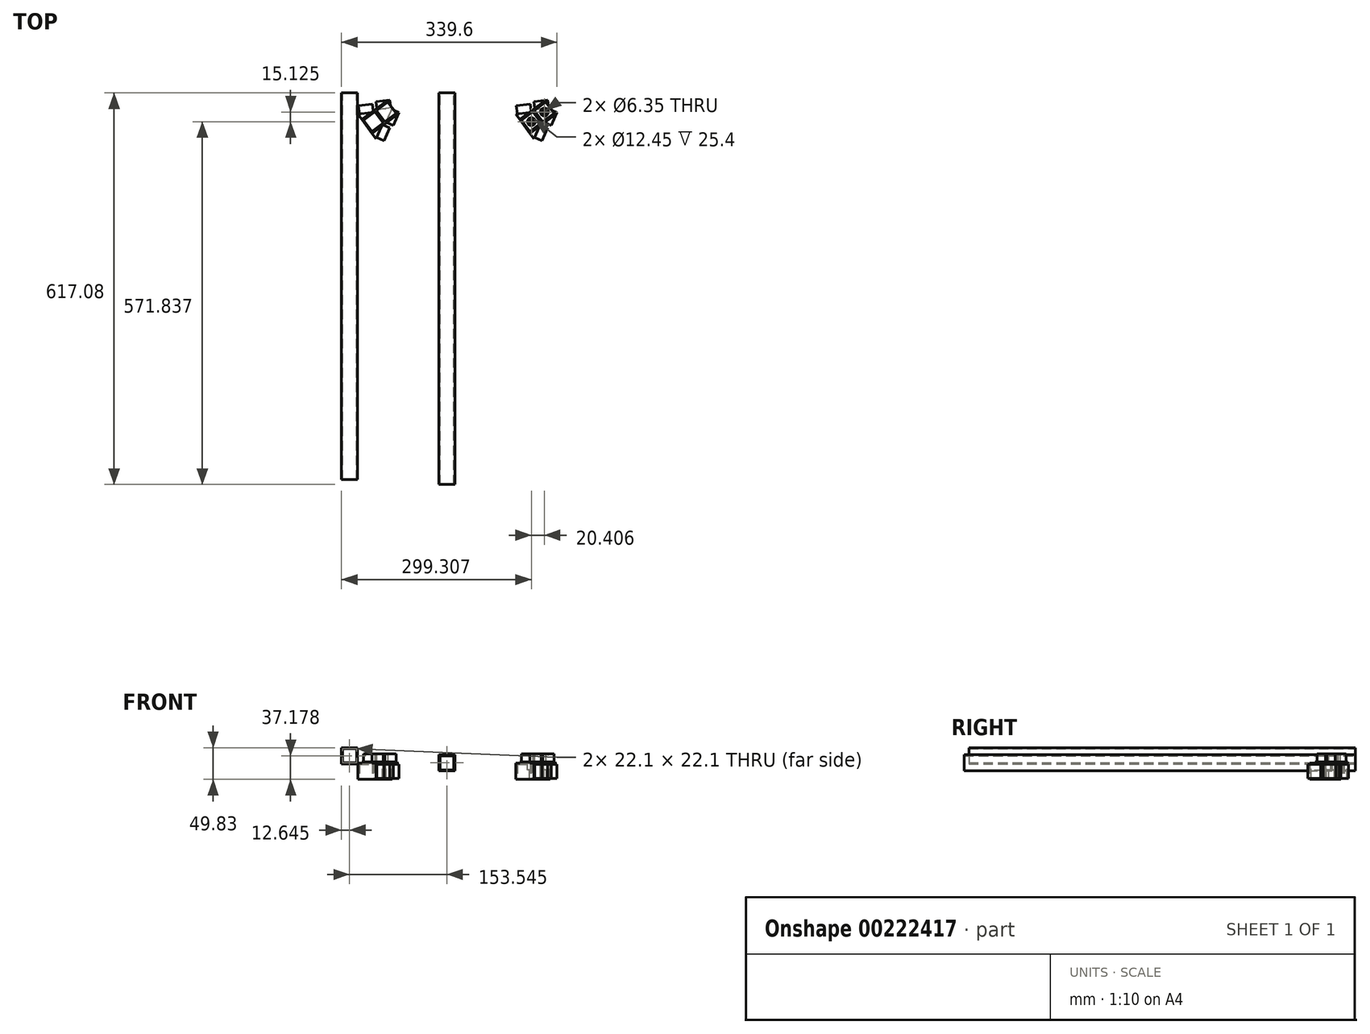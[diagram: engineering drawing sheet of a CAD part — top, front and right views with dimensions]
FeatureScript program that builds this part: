
annotation { "Feature Type Name" : "Feature", "Feature Type Description" : "" }
export const myFeature = defineFeature(function(context is Context, id is Id, definition is map)
    precondition{}
    {
        {
            var Q0;
            Q0=qCreatedBy(makeId("Front.planeOp"),FACE);
            var sketch = newSketch(context, id + "F0", { "sketchPlane" : qUnion([Q0])});
            skLineSegment(sketch, "E0.bottom", {"start": v(-114.26, 49.83) * mm, "end": v(-88.97, 49.83) * mm});
            skLineSegment(sketch, "E0.top", {"start": v(-114.26, 24.53) * mm, "end": v(-88.97, 24.53) * mm});
            skLineSegment(sketch, "E0.left", {"start": v(-114.26, 49.83) * mm, "end": v(-114.26, 24.53) * mm});
            skLineSegment(sketch, "E0.right", {"start": v(-88.97, 49.83) * mm, "end": v(-88.97, 24.53) * mm});
            skLineSegment(sketch, "E1.bottom", {"start": v(-112.66, 48.23) * mm, "end": v(-90.57, 48.23) * mm});
            skLineSegment(sketch, "E1.top", {"start": v(-112.66, 26.13) * mm, "end": v(-90.57, 26.13) * mm});
            skLineSegment(sketch, "E1.left", {"start": v(-112.66, 48.23) * mm, "end": v(-112.66, 26.13) * mm});
            skLineSegment(sketch, "E1.right", {"start": v(-90.57, 48.23) * mm, "end": v(-90.57, 26.13) * mm});
            skSolve(sketch);
        }
        {
            var Q0;
            Q0=makeQuery(id+"F0.imprint","IMPRINT",FACE,{"disambiguationData":[TD([[makeQuery(id+"F0.imprint","IMPRINT",EDGE,{"derivedFrom":sQuery(id+"F0.wireOp",EDGE,"E0.bottom")}),-1.0]])]});
            extrude(context, id + "F1", {"entities" : qUnion([Q0]), "depth" : 609.6 * mm});
        }
        {
            var Q0;
            Q0=qCreatedBy(makeId("Top.planeOp"),FACE);
            var sketch = newSketch(context, id + "F2", { "sketchPlane" : qUnion([Q0])});
            skLineSegment(sketch, "E2", {"start": v(-61.22, -26.36) * mm, "end": v(-45.03, -48.2) * mm});
            skLineSegment(sketch, "E3", {"start": v(-45.03, -48.2) * mm, "end": v(-34.22, -23.26) * mm});
            skLineSegment(sketch, "E4", {"start": v(-34.22, -23.26) * mm, "end": v(-61.22, -26.36) * mm});
            skSolve(sketch);
        }
        {
            var Q0;
            Q0=makeQuery(id+"F2.imprint","IMPRINT",FACE,{"disambiguationData":[TD([[makeQuery(id+"F2.imprint","IMPRINT",EDGE,{"derivedFrom":sQuery(id+"F2.wireOp",EDGE,"E2")}),1.0]])]});
            extrude(context, id + "F3", {"entities" : qUnion([Q0]), "depth" : 25.4 * mm});
        }
        {
            var Q0;
            Q0=makeQuery(id+"F3.opExtrude","SWEPT_FACE",FACE,{"disambiguationData":[OSD([sQuery(id+"F2.wireOp",EDGE,"E4")])]});
            var sketch = newSketch(context, id + "F4", { "sketchPlane" : qUnion([Q0])});
            skLineSegment(sketch, "E5.bottom", {"start": v(61.28, 1.65) * mm, "end": v(39.19, 1.65) * mm});
            skLineSegment(sketch, "E5.top", {"start": v(61.28, 23.75) * mm, "end": v(39.19, 23.75) * mm});
            skLineSegment(sketch, "E5.left", {"start": v(61.28, 1.65) * mm, "end": v(61.28, 23.75) * mm});
            skLineSegment(sketch, "E5.right", {"start": v(39.19, 1.65) * mm, "end": v(39.19, 23.75) * mm});
            skSolve(sketch);
        }
        {
            var Q0;
            Q0=makeQuery(id+"F4.imprint","IMPRINT",FACE,{"disambiguationData":[TD([[makeQuery(id+"F4.imprint","IMPRINT",EDGE,{"derivedFrom":sQuery(id+"F4.wireOp",EDGE,"E5.bottom")}),-1.0]])]});
            extrude(context, id + "F5", {"entities" : qUnion([Q0]), "operationType" : NewBodyOperationType.ADD, "depth" : 12.7 * mm});
        }
        {
            var Q0;
            Q0=makeQuery(id+"F3.opExtrude","SWEPT_FACE",FACE,{"disambiguationData":[OSD([sQuery(id+"F2.wireOp",EDGE,"E3")])]});
            var sketch = newSketch(context, id + "F6", { "sketchPlane" : qUnion([Q0])});
            skLineSegment(sketch, "E6.bottom", {"start": v(-37.5, 1.65) * mm, "end": v(-59.6, 1.65) * mm});
            skLineSegment(sketch, "E6.top", {"start": v(-37.5, 23.75) * mm, "end": v(-59.6, 23.75) * mm});
            skLineSegment(sketch, "E6.left", {"start": v(-37.5, 1.65) * mm, "end": v(-37.5, 23.75) * mm});
            skLineSegment(sketch, "E6.right", {"start": v(-59.6, 1.65) * mm, "end": v(-59.6, 23.75) * mm});
            skSolve(sketch);
        }
        {
            var Q0;
            Q0=makeQuery(id+"F6.imprint","IMPRINT",FACE,{"disambiguationData":[TD([[makeQuery(id+"F6.imprint","IMPRINT",EDGE,{"derivedFrom":sQuery(id+"F6.wireOp",EDGE,"E6.bottom")}),-1.0]])]});
            extrude(context, id + "F7", {"entities" : qUnion([Q0]), "operationType" : NewBodyOperationType.ADD, "depth" : 12.7 * mm});
        }
        {
            var Q0;
            Q0=makeQuery(id+"F3.opExtrude","SWEPT_FACE",FACE,{"disambiguationData":[OSD([sQuery(id+"F2.wireOp",EDGE,"E2")])]});
            var sketch = newSketch(context, id + "F8", { "sketchPlane" : qUnion([Q0])});
            skLineSegment(sketch, "E7.bottom", {"start": v(-15.28, 25.4) * mm, "end": v(11.9, 25.4) * mm});
            skLineSegment(sketch, "E7.top", {"start": v(-15.28, 0) * mm, "end": v(11.9, 0) * mm});
            skLineSegment(sketch, "E7.left", {"start": v(-15.28, 25.4) * mm, "end": v(-15.28, 0) * mm});
            skLineSegment(sketch, "E7.right", {"start": v(11.9, 25.4) * mm, "end": v(11.9, 0) * mm});
            skPoint(sketch, "E7.middle", {"position": v(-1.69, 12.7) * mm});
            skPoint(sketch, "E7.middle.positionSnap0", {"position": v(-1.69, 0) * mm});
            skPoint(sketch, "E7.middle.positionSnap1", {"position": v(11.9, 12.7) * mm});
            skPoint(sketch, "E7.centerSnap0", {"position": v(-1.69, 0) * mm});
            skPoint(sketch, "E7.centerSnap1", {"position": v(11.9, 12.7) * mm});
            skSolve(sketch);
        }
        {
            var Q0;
            Q0=makeQuery(id+"F8.imprint","IMPRINT",FACE,{"disambiguationData":[TD([[makeQuery(id+"F8.imprint","IMPRINT",EDGE,{"derivedFrom":sQuery(id+"F8.wireOp",EDGE,"E7.bottom")}),-1.0]])]});
            extrude(context, id + "F9", {"entities" : qUnion([Q0]), "operationType" : NewBodyOperationType.ADD, "depth" : 2.54 * mm});
        }
        {
            var Q0;
            Q0=makeQuery(id+"F9.boolean.opBoolean","MERGE",FACE,{"derivedFrom":[makeQuery(id+"F3.opExtrude","CAP_FACE",FACE,{"disambiguationData":[OSD([sQuery(id+"F2.wireOp",EDGE,"E2"),sQuery(id+"F2.wireOp",EDGE,"E3"),sQuery(id+"F2.wireOp",EDGE,"E4")])],"isStart":true}),makeQuery(id+"F9.opExtrude","SWEPT_FACE",FACE,{"disambiguationData":[OSD([sQuery(id+"F8.wireOp",EDGE,"E7.top")])]})]});
            var sketch = newSketch(context, id + "F10", { "sketchPlane" : qUnion([Q0])});
            skLineSegment(sketch, "E8", {"start": v(-61.56, 30.16) * mm, "end": v(-88.56, 33.26) * mm});
            skLineSegment(sketch, "E9", {"start": v(-88.56, 33.26) * mm, "end": v(-59.59, 72.35) * mm});
            skLineSegment(sketch, "E10", {"start": v(-59.59, 72.35) * mm, "end": v(-48.77, 47.42) * mm});
            skLineSegment(sketch, "E11", {"start": v(-48.77, 47.42) * mm, "end": v(-61.56, 30.16) * mm});
            skSolve(sketch);
        }
        {
            var Q0;
            Q0=makeQuery(id+"F10.imprint","IMPRINT",FACE,{"disambiguationData":[TD([[makeQuery(id+"F10.imprint","IMPRINT",EDGE,{"derivedFrom":sQuery(id+"F10.wireOp",EDGE,"E8")}),-1.0]])]});
            extrude(context, id + "F11", {"entities" : qUnion([Q0]), "oppositeDirection" : true, "depth" : 25.4 * mm});
        }
        {
            var Q0;
            Q0=makeQuery(id+"F3.opExtrude","SWEPT_BODY",BODY,{"disambiguationData":[OSD([sQuery(id+"F2.wireOp",EDGE,"E2"),sQuery(id+"F2.wireOp",EDGE,"E3"),sQuery(id+"F2.wireOp",EDGE,"E4")])]});
            var Q1;
            Q1=makeQuery(id+"F11.opExtrude","SWEPT_BODY",BODY,{"disambiguationData":[OSD([sQuery(id+"F10.wireOp",EDGE,"E8"),sQuery(id+"F10.wireOp",EDGE,"E9"),sQuery(id+"F10.wireOp",EDGE,"E10"),sQuery(id+"F10.wireOp",EDGE,"E11"),sQuery(id+"F10.wireOp",EDGE,"Vaxxx6k1-s7dE-GzpN-L4S0-QTjSZHgLK0QL"),sQuery(id+"F10.wireOp",EDGE,"sgtSGyO8-zE94-4HEN-QIov-kYSwHspXC1a0"),sQuery(id+"F10.wireOp",EDGE,"E74jwKx9-sHOy-HuwW-fk9N-56BErMT5pzip"),sQuery(id+"F10.wireOp",EDGE,"OfEb48GK-fXVu-JcS2-bLEe-MdiGg9vhfpWM")])]});
            booleanBodies(context, id + "F12", {"operationType" : BooleanOperationType.UNION, "tools" : qUnion([Q0, Q1])});
        }
        {
            var Q0;
            Q0=makeQuery(id+"F11.opExtrude","SWEPT_FACE",FACE,{"disambiguationData":[OSD([sQuery(id+"F10.wireOp",EDGE,"E8")])]});
            var sketch = newSketch(context, id + "F13", { "sketchPlane" : qUnion([Q0])});
            skLineSegment(sketch, "E12.bottom", {"start": v(89.24, 23.75) * mm, "end": v(67.14, 23.75) * mm});
            skLineSegment(sketch, "E12.top", {"start": v(89.24, 1.65) * mm, "end": v(67.14, 1.65) * mm});
            skLineSegment(sketch, "E12.left", {"start": v(89.24, 23.75) * mm, "end": v(89.24, 1.65) * mm});
            skLineSegment(sketch, "E12.right", {"start": v(67.14, 23.75) * mm, "end": v(67.14, 1.65) * mm});
            skPoint(sketch, "E12.middle", {"position": v(78.19, 12.7) * mm});
            skSolve(sketch);
        }
        {
            var Q0;
            Q0=makeQuery(id+"F13.imprint","IMPRINT",FACE,{"disambiguationData":[TD([[makeQuery(id+"F13.imprint","IMPRINT",EDGE,{"derivedFrom":sQuery(id+"F13.wireOp",EDGE,"E12.bottom")}),1.0]])]});
            extrude(context, id + "F14", {"entities" : qUnion([Q0]), "operationType" : NewBodyOperationType.ADD, "depth" : 12.7 * mm});
        }
        {
            var Q0;
            Q0=makeQuery(id+"F11.opExtrude","SWEPT_FACE",FACE,{"disambiguationData":[OSD([sQuery(id+"F10.wireOp",EDGE,"E10")])]});
            var sketch = newSketch(context, id + "F15", { "sketchPlane" : qUnion([Q0])});
            skLineSegment(sketch, "E13.bottom", {"start": v(-87.55, 1.65) * mm, "end": v(-65.45, 1.65) * mm});
            skLineSegment(sketch, "E13.top", {"start": v(-87.55, 23.75) * mm, "end": v(-65.45, 23.75) * mm});
            skLineSegment(sketch, "E13.left", {"start": v(-87.55, 1.65) * mm, "end": v(-87.55, 23.75) * mm});
            skLineSegment(sketch, "E13.right", {"start": v(-65.45, 1.65) * mm, "end": v(-65.45, 23.75) * mm});
            skPoint(sketch, "E13.middle", {"position": v(-76.5, 12.7) * mm});
            skSolve(sketch);
        }
        {
            var Q0;
            Q0=makeQuery(id+"F15.imprint","IMPRINT",FACE,{"disambiguationData":[TD([[makeQuery(id+"F15.imprint","IMPRINT",EDGE,{"derivedFrom":sQuery(id+"F15.wireOp",EDGE,"E13.bottom")}),1.0]])]});
            extrude(context, id + "F16", {"entities" : qUnion([Q0]), "operationType" : NewBodyOperationType.ADD, "depth" : 12.7 * mm});
        }
        {
            var Q0;
            Q0=makeQuery(id+"F12.opBoolean","MERGE",FACE,{"derivedFrom":[makeQuery(id+"F9.boolean.opBoolean","MERGE",FACE,{"derivedFrom":[makeQuery(id+"F3.opExtrude","CAP_FACE",FACE,{"disambiguationData":[OSD([sQuery(id+"F2.wireOp",EDGE,"E2"),sQuery(id+"F2.wireOp",EDGE,"E3"),sQuery(id+"F2.wireOp",EDGE,"E4")])],"isStart":false}),makeQuery(id+"F9.opExtrude","SWEPT_FACE",FACE,{"disambiguationData":[OSD([sQuery(id+"F8.wireOp",EDGE,"E7.bottom")])]})]}),makeQuery(id+"F11.opExtrude","CAP_FACE",FACE,{"disambiguationData":[OSD([sQuery(id+"F10.wireOp",EDGE,"E8"),sQuery(id+"F10.wireOp",EDGE,"E9"),sQuery(id+"F10.wireOp",EDGE,"E10"),sQuery(id+"F10.wireOp",EDGE,"E11")])],"isStart":false})]});
            var sketch = newSketch(context, id + "F17", { "sketchPlane" : qUnion([Q0])});
            skLineSegment(sketch, "E14", {"start": v(-65.98, -63.72) * mm, "end": v(-82.17, -41.89) * mm});
            skLineSegment(sketch, "E15", {"start": v(-82.17, -41.89) * mm, "end": v(-42.58, -12.55) * mm});
            skLineSegment(sketch, "E16", {"start": v(-42.58, -12.55) * mm, "end": v(-26.4, -34.38) * mm});
            skLineSegment(sketch, "E17", {"start": v(-26.4, -34.38) * mm, "end": v(-65.98, -63.72) * mm});
            skSolve(sketch);
        }
        {
            var Q0;
            {var subQ24=sQuery(id+"F17.wireOp",EDGE,"E14");Q0=makeQuery(id+"F17.imprint","IMPRINT",FACE,{"disambiguationData":[TD([[makeQuery(id+"F17.imprint","IMPRINT",EDGE,{"derivedFrom":subQ24}),1.0]])]});}
            var Q1;
            {var subQ0=sQuery(id+"F17.wireOp",EDGE,"E17");var subQ1=sQuery(id+"F17.wireOp",EDGE,"E16");var subQ2=makeQuery(id+"F17.imprint","INTERSECT",VERTEX,{"derivedFrom":[subQ1,subQ0]});Q1=makeQuery(id+"F17.imprint","IMPRINT",FACE,{"disambiguationData":[TD([[makeQuery(id+"F17.imprint","IMPRINT",EDGE,{"disambiguationData":[TD([[subQ2,1.0]])],"derivedFrom":subQ1}),-1.0]])]});}
            var Q2;
            {var subQ0=sQuery(id+"F17.wireOp",EDGE,"E15");var subQ1=makeQuery(id+"F3.opExtrude","CAP_EDGE",EDGE,{"disambiguationData":[OSD([sQuery(id+"F2.wireOp",EDGE,"E4")])],"isStart":false});var subQ2=makeQuery(id+"F17.imprint","INTERSECT",VERTEX,{"derivedFrom":[subQ1,subQ0]});Q2=makeQuery(id+"F17.imprint","IMPRINT",FACE,{"disambiguationData":[TD([[makeQuery(id+"F17.imprint","IMPRINT",EDGE,{"disambiguationData":[TD([[subQ2,-1.0]])],"derivedFrom":subQ0}),-1.0]])]});}
            var Q3;
            {var subQ1=sQuery(id+"F8.wireOp",EDGE,"E7.left");var subQ2=sQuery(id+"F8.wireOp",EDGE,"E7.bottom");var subQ4=makeQuery(id+"F12.opBoolean","SPLIT",EDGE,{"disambiguationData":[TD([makeQuery(id+"F9.opExtrude","SWEPT_FACE",FACE,{"disambiguationData":[OSD([subQ1])]})])],"derivedFrom":makeQuery(id+"F9.opExtrude","CAP_EDGE",EDGE,{"disambiguationData":[OSD([subQ2])],"isStart":false})});Q3=makeQuery(id+"F17.imprint","IMPRINT",FACE,{"disambiguationData":[TD([[makeQuery(id+"F17.imprint","IMPRINT",EDGE,{"derivedFrom":subQ4}),-1.0]])]});}
            var Q4;
            {var subQ1=sQuery(id+"F8.wireOp",EDGE,"E7.right");var subQ3=sQuery(id+"F8.wireOp",EDGE,"E7.bottom");var subQ4=makeQuery(id+"F12.opBoolean","SPLIT",EDGE,{"disambiguationData":[TD([makeQuery(id+"F9.opExtrude","SWEPT_FACE",FACE,{"disambiguationData":[OSD([subQ1])]})])],"derivedFrom":makeQuery(id+"F9.opExtrude","CAP_EDGE",EDGE,{"disambiguationData":[OSD([subQ3])],"isStart":false})});Q4=makeQuery(id+"F17.imprint","IMPRINT",FACE,{"disambiguationData":[TD([[makeQuery(id+"F17.imprint","IMPRINT",EDGE,{"derivedFrom":subQ4}),-1.0]])]});}
            extrude(context, id + "F18", {"entities" : qUnion([Q0, Q1, Q2, Q3, Q4]), "operationType" : NewBodyOperationType.ADD, "depth" : 1.78 * mm});
        }
        {
            var Q0;
            Q0=makeQuery(id+"F18.opExtrude","CAP_FACE",FACE,{"disambiguationData":[OSD([sQuery(id+"F17.wireOp",EDGE,"E14"),sQuery(id+"F17.wireOp",EDGE,"E15"),sQuery(id+"F17.wireOp",EDGE,"E16"),sQuery(id+"F17.wireOp",EDGE,"E17")])],"isStart":false});
            var sketch = newSketch(context, id + "F19", { "sketchPlane" : qUnion([Q0])});
            skLineSegment(sketch, "E18.bottom", {"start": v(-48.42, -47.54) * mm, "end": v(-61.58, -29.79) * mm});
            skLineSegment(sketch, "E18.top", {"start": v(-66.17, -60.7) * mm, "end": v(-79.33, -42.95) * mm});
            skLineSegment(sketch, "E18.left", {"start": v(-48.42, -47.54) * mm, "end": v(-66.17, -60.7) * mm});
            skLineSegment(sketch, "E18.right", {"start": v(-61.58, -29.79) * mm, "end": v(-79.33, -42.95) * mm});
            skPoint(sketch, "E18.middle", {"position": v(-63.87, -45.24) * mm});
            skLineSegment(sketch, "E19.bottom", {"start": v(-28.01, -32.41) * mm, "end": v(-45.76, -45.57) * mm});
            skLineSegment(sketch, "E19.top", {"start": v(-41.17, -14.66) * mm, "end": v(-58.92, -27.82) * mm});
            skLineSegment(sketch, "E19.left", {"start": v(-28.01, -32.41) * mm, "end": v(-41.17, -14.66) * mm});
            skLineSegment(sketch, "E19.right", {"start": v(-45.76, -45.57) * mm, "end": v(-58.92, -27.82) * mm});
            skPoint(sketch, "E19.middle", {"position": v(-43.47, -30.12) * mm});
            skSolve(sketch);
        }
        {
            var Q0;
            Q0=makeQuery(id+"F19.imprint","IMPRINT",FACE,{"disambiguationData":[TD([[makeQuery(id+"F19.imprint","IMPRINT",EDGE,{"derivedFrom":sQuery(id+"F19.wireOp",EDGE,"E18.bottom")}),1.0]])]});
            var Q1;
            {var subQ0=sQuery(id+"F19.wireOp",EDGE,"E19.right");Q1=makeQuery(id+"F19.imprint","IMPRINT",FACE,{"disambiguationData":[TD([[makeQuery(id+"F19.imprint","IMPRINT",EDGE,{"derivedFrom":subQ0}),-1.0]])]});}
            var Q2;
            {var subQ0=sQuery(id+"F19.wireOp",EDGE,"E19.left");var subQ1=sQuery(id+"F19.wireOp",EDGE,"E19.bottom");var subQ2=makeQuery(id+"F19.imprint","INTERSECT",VERTEX,{"derivedFrom":[subQ1,subQ0]});Q2=makeQuery(id+"F19.imprint","IMPRINT",FACE,{"disambiguationData":[TD([[makeQuery(id+"F19.imprint","IMPRINT",EDGE,{"disambiguationData":[TD([[subQ2,-1.0]])],"derivedFrom":subQ1}),-1.0]])]});}
            var Q3;
            {var subQ0=sQuery(id+"F19.wireOp",EDGE,"E19.left");var subQ1=sQuery(id+"F19.wireOp",EDGE,"E19.top");var subQ2=makeQuery(id+"F19.imprint","INTERSECT",VERTEX,{"derivedFrom":[subQ1,subQ0]});Q3=makeQuery(id+"F19.imprint","IMPRINT",FACE,{"disambiguationData":[TD([[makeQuery(id+"F19.imprint","IMPRINT",EDGE,{"disambiguationData":[TD([[subQ2,-1.0]])],"derivedFrom":subQ1}),1.0]])]});}
            extrude(context, id + "F20", {"entities" : qUnion([Q0, Q1, Q2, Q3]), "operationType" : NewBodyOperationType.ADD, "depth" : 12.7 * mm});
        }
        {
            var Q0;
            Q0=makeQuery(id+"F3.opExtrude","SWEPT_BODY",BODY,{"disambiguationData":[OSD([sQuery(id+"F2.wireOp",EDGE,"E2"),sQuery(id+"F2.wireOp",EDGE,"E3"),sQuery(id+"F2.wireOp",EDGE,"E4")])]});
            transform(context, id + "F21", {"entities" : qUnion([Q0]), "transformType" : TransformType.TRANSLATION_3D, "dx" : 248.92 * mm, "dy" : 0 * mm, "dz" : 0 * mm, "makeCopy" : true});
        }
        {
            var Q0;
            Q0=makeQuery(id+"F21.opPattern","COPY",FACE,{"derivedFrom":makeQuery(id+"F20.opExtrude","CAP_FACE",FACE,{"disambiguationData":[OSD([sQuery(id+"F19.wireOp",EDGE,"E19.bottom"),sQuery(id+"F19.wireOp",EDGE,"E19.top"),sQuery(id+"F19.wireOp",EDGE,"E19.left"),sQuery(id+"F19.wireOp",EDGE,"E19.right")])],"isStart":false}),"instanceName":"1"});
            var sketch = newSketch(context, id + "F22", { "sketchPlane" : qUnion([Q0])});
            skCircle(sketch, "E20", {"center": v(205.45, -30.12) * mm, "radius": 3.18 * mm});
            skSolve(sketch);
        }
        {
            var Q0;
            Q0=makeQuery(id+"F21.opPattern","COPY",FACE,{"derivedFrom":makeQuery(id+"F20.opExtrude","CAP_FACE",FACE,{"disambiguationData":[OSD([sQuery(id+"F19.wireOp",EDGE,"E18.bottom"),sQuery(id+"F19.wireOp",EDGE,"E18.top"),sQuery(id+"F19.wireOp",EDGE,"E18.left"),sQuery(id+"F19.wireOp",EDGE,"E18.right")])],"isStart":false}),"instanceName":"1"});
            var sketch = newSketch(context, id + "F23", { "sketchPlane" : qUnion([Q0])});
            skCircle(sketch, "E21", {"center": v(185.05, -45.24) * mm, "radius": 3.18 * mm});
            skSolve(sketch);
        }
        {
            var Q0;
            Q0=makeQuery(id+"F22.imprint","IMPRINT",FACE,{"disambiguationData":[TD([[makeQuery(id+"F22.imprint","IMPRINT",EDGE,{"derivedFrom":sQuery(id+"F22.wireOp",EDGE,"E20")}),1.0]])]});
            var Q1;
            Q1=makeQuery(id+"F23.imprint","IMPRINT",FACE,{"disambiguationData":[TD([[makeQuery(id+"F23.imprint","IMPRINT",EDGE,{"derivedFrom":sQuery(id+"F23.wireOp",EDGE,"E21")}),1.0]])]});
            extrude(context, id + "F24", {"entities" : qUnion([Q0, Q1]), "operationType" : NewBodyOperationType.REMOVE, "oppositeDirection" : true, "depth" : 50.8 * mm});
        }
        {
            var Q0;
            Q0=makeQuery(id+"F21.opPattern","COPY",FACE,{"derivedFrom":makeQuery(id+"F20.opExtrude","CAP_FACE",FACE,{"disambiguationData":[OSD([sQuery(id+"F19.wireOp",EDGE,"E19.bottom"),sQuery(id+"F19.wireOp",EDGE,"E19.top"),sQuery(id+"F19.wireOp",EDGE,"E19.left"),sQuery(id+"F19.wireOp",EDGE,"E19.right")])],"isStart":false}),"instanceName":"1"});
            var sketch = newSketch(context, id + "F25", { "sketchPlane" : qUnion([Q0])});
            skCircle(sketch, "E22", {"center": v(205.45, -30.12) * mm, "radius": 6.22 * mm});
            skSolve(sketch);
        }
        {
            var Q0;
            Q0=makeQuery(id+"F21.opPattern","COPY",FACE,{"derivedFrom":makeQuery(id+"F20.opExtrude","CAP_FACE",FACE,{"disambiguationData":[OSD([sQuery(id+"F19.wireOp",EDGE,"E18.bottom"),sQuery(id+"F19.wireOp",EDGE,"E18.top"),sQuery(id+"F19.wireOp",EDGE,"E18.left"),sQuery(id+"F19.wireOp",EDGE,"E18.right")])],"isStart":false}),"instanceName":"1"});
            var sketch = newSketch(context, id + "F26", { "sketchPlane" : qUnion([Q0])});
            skCircle(sketch, "E23", {"center": v(185.05, -45.24) * mm, "radius": 6.22 * mm});
            skSolve(sketch);
        }
        {
            var Q0;
            Q0=makeQuery(id+"F26.imprint","IMPRINT",FACE,{"disambiguationData":[TD([[makeQuery(id+"F26.imprint","IMPRINT",EDGE,{"derivedFrom":sQuery(id+"F26.wireOp",EDGE,"E23")}),1.0]])]});
            var Q1;
            Q1=makeQuery(id+"F25.imprint","IMPRINT",FACE,{"disambiguationData":[TD([[makeQuery(id+"F25.imprint","IMPRINT",EDGE,{"derivedFrom":sQuery(id+"F25.wireOp",EDGE,"E22")}),1.0]])]});
            extrude(context, id + "F27", {"entities" : qUnion([Q0, Q1]), "operationType" : NewBodyOperationType.REMOVE, "oppositeDirection" : true, "depth" : 25.4 * mm});
        }
        {
            var Q0;
            Q0=qCreatedBy(makeId("Front.planeOp"),FACE);
            var sketch = newSketch(context, id + "F28", { "sketchPlane" : qUnion([Q0])});
            skLineSegment(sketch, "E24.bottom", {"start": v(64.58, 38.65) * mm, "end": v(39.28, 38.65) * mm});
            skLineSegment(sketch, "E24.top", {"start": v(64.58, 13.35) * mm, "end": v(39.28, 13.35) * mm});
            skLineSegment(sketch, "E24.left", {"start": v(64.58, 38.65) * mm, "end": v(64.58, 13.35) * mm});
            skLineSegment(sketch, "E24.right", {"start": v(39.28, 38.65) * mm, "end": v(39.28, 13.35) * mm});
            skLineSegment(sketch, "E25.bottom", {"start": v(40.88, 37.05) * mm, "end": v(62.98, 37.05) * mm});
            skLineSegment(sketch, "E25.top", {"start": v(40.88, 14.95) * mm, "end": v(62.98, 14.95) * mm});
            skLineSegment(sketch, "E25.left", {"start": v(40.88, 37.05) * mm, "end": v(40.88, 14.95) * mm});
            skLineSegment(sketch, "E25.right", {"start": v(62.98, 37.05) * mm, "end": v(62.98, 14.95) * mm});
            skSolve(sketch);
        }
        {
            var Q0;
            Q0 = qSketchRegion(id + "F28", true);
            extrude(context, id + "F29", {"entities" : qUnion([Q0]), "depth" : 617.08 * mm});
        }
    });
